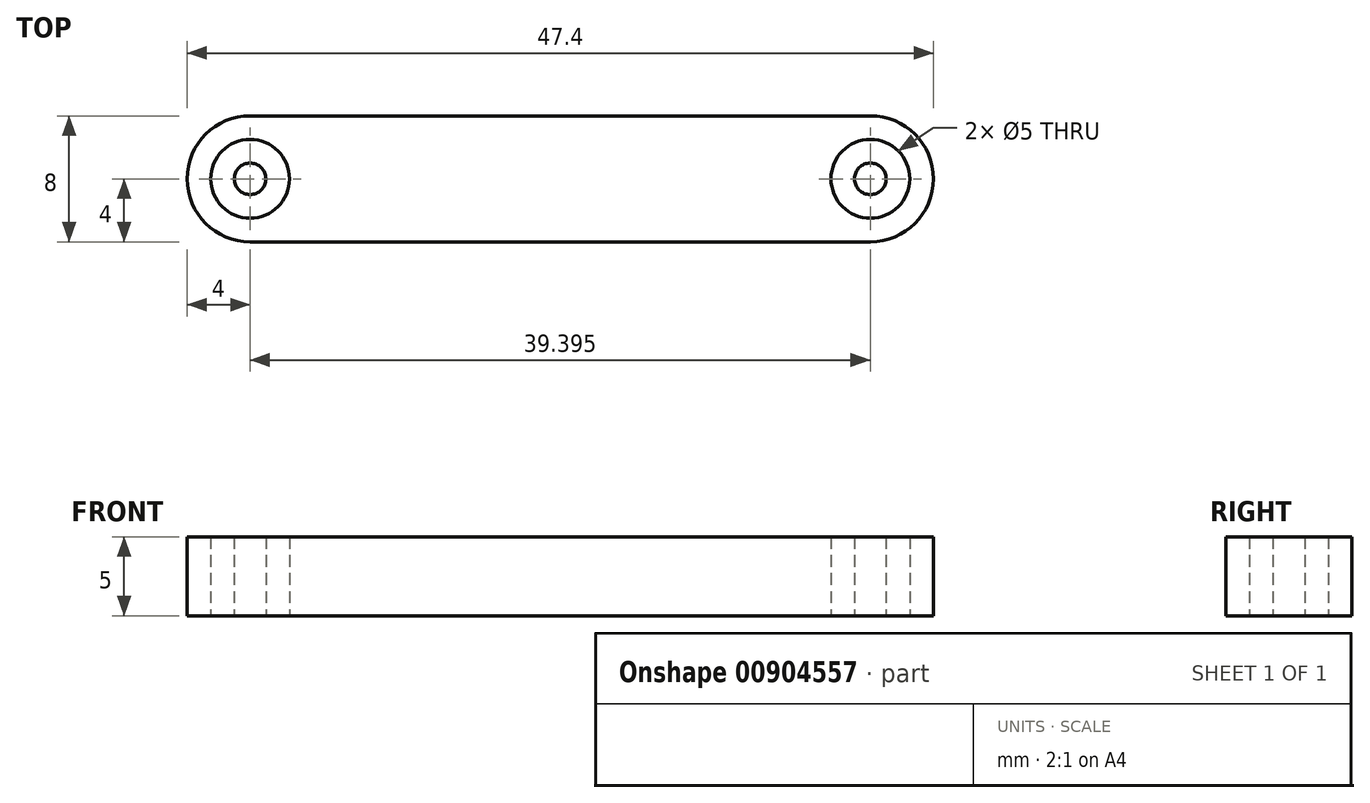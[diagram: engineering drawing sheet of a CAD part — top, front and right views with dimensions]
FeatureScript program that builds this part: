
annotation { "Feature Type Name" : "Feature", "Feature Type Description" : "" }
export const myFeature = defineFeature(function(context is Context, id is Id, definition is map)
    precondition{}
    {
        {
            var Q0;
            Q0=qCreatedBy(makeId("Top.planeOp"),FACE);
            var sketch = newSketch(context, id + "F0", { "sketchPlane" : qUnion([Q0])});
            skCircle(sketch, "E0", {"center": v(0, 0) * mm, "radius": 2.5 * mm});
            skCircle(sketch, "E1", {"center": v(39.4, 0) * mm, "radius": 2.5 * mm});
            skCircle(sketch, "E2", {"center": v(0, 0) * mm, "radius": 1 * mm});
            skCircle(sketch, "E3", {"center": v(39.4, 0) * mm, "radius": 1 * mm});
            skArc(sketch, "E4", {"start": v(0, 4) * mm, "mid": v(-4, 0) * mm, "end": v(0, -4) * mm});
            skArc(sketch, "E5", {"start": v(39.4, -4) * mm, "mid": v(43.4, 0) * mm, "end": v(39.4, 4) * mm});
            skLineSegment(sketch, "E6", {"start": v(0, 4) * mm, "end": v(39.4, 4) * mm});
            skLineSegment(sketch, "E7", {"start": v(0, -4) * mm, "end": v(39.4, -4) * mm});
            skSolve(sketch);
        }
        {
            var Q0;
            Q0=makeQuery(id+"F0.imprint","IMPRINT",FACE,{"disambiguationData":[TD([[makeQuery(id+"F0.imprint","IMPRINT",EDGE,{"derivedFrom":sQuery(id+"F0.wireOp",EDGE,"E2")}),1.0]])]});
            var Q1;
            Q1=makeQuery(id+"F0.imprint","IMPRINT",FACE,{"disambiguationData":[TD([[makeQuery(id+"F0.imprint","IMPRINT",EDGE,{"derivedFrom":sQuery(id+"F0.wireOp",EDGE,"E3")}),1.0]])]});
            var Q2;
            Q2=makeQuery(id+"F0.imprint","IMPRINT",FACE,{"disambiguationData":[TD([[makeQuery(id+"F0.imprint","IMPRINT",EDGE,{"derivedFrom":sQuery(id+"F0.wireOp",EDGE,"E0")}),-1.0]])]});
            extrude(context, id + "F1", {"entities" : qUnion([Q0, Q1, Q2]), "endBound" : BoundingType.SYMMETRIC, "depth" : 5 * mm, "offsetDistance" : 25.4 * mm});
        }
    });
